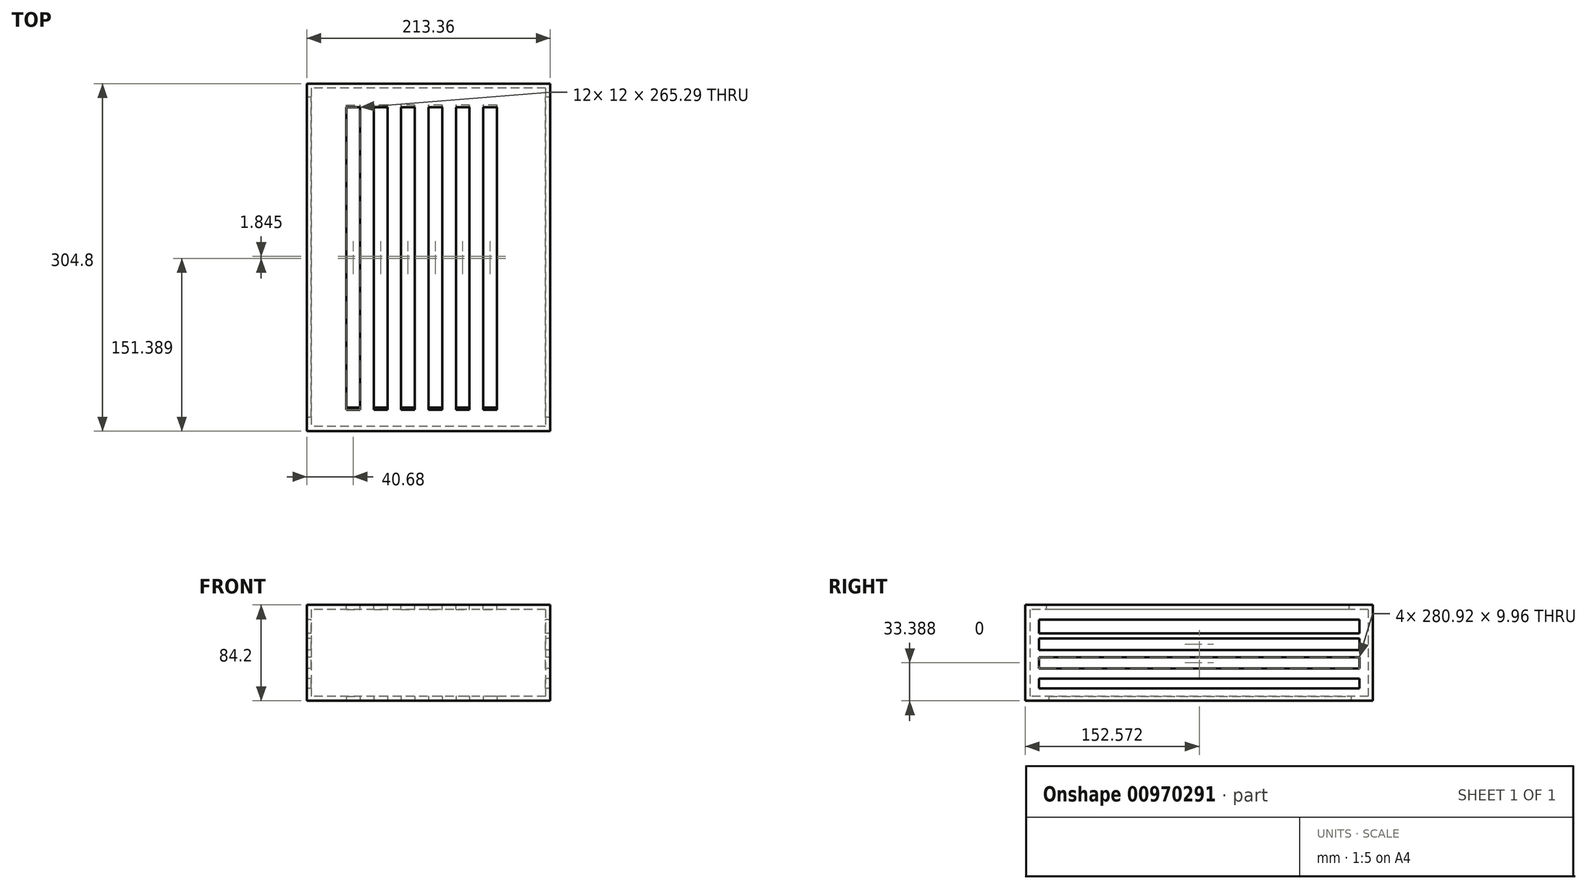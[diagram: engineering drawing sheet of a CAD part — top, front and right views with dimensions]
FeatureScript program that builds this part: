
annotation { "Feature Type Name" : "Feature", "Feature Type Description" : "" }
export const myFeature = defineFeature(function(context is Context, id is Id, definition is map)
    precondition{}
    {
        {
            var Q0;
            Q0=qCreatedBy(makeId("Top.planeOp"),FACE);
            var sketch = newSketch(context, id + "F0", { "sketchPlane" : qUnion([Q0])});
            skLineSegment(sketch, "E0.bottom", {"start": v(106.68, 152.4) * mm, "end": v(-106.68, 152.4) * mm});
            skLineSegment(sketch, "E0.top", {"start": v(106.68, -152.4) * mm, "end": v(-106.68, -152.4) * mm});
            skLineSegment(sketch, "E0.left", {"start": v(106.68, 152.4) * mm, "end": v(106.68, -152.4) * mm});
            skLineSegment(sketch, "E0.right", {"start": v(-106.68, 152.4) * mm, "end": v(-106.68, -152.4) * mm});
            skPoint(sketch, "E0.middle", {"position": v(0, 0) * mm});
            skLineSegment(sketch, "E1.bottom", {"start": v(102.68, 148.4) * mm, "end": v(-102.68, 148.4) * mm});
            skLineSegment(sketch, "E1.top", {"start": v(102.68, -148.4) * mm, "end": v(-102.68, -148.4) * mm});
            skLineSegment(sketch, "E1.left", {"start": v(102.68, 148.4) * mm, "end": v(102.68, -148.4) * mm});
            skLineSegment(sketch, "E1.right", {"start": v(-102.68, 148.4) * mm, "end": v(-102.68, -148.4) * mm});
            skSolve(sketch);
        }
        {
            var Q0;
            Q0=makeQuery(id+"F0.imprint","IMPRINT",FACE,{"disambiguationData":[TD([[makeQuery(id+"F0.imprint","IMPRINT",EDGE,{"derivedFrom":sQuery(id+"F0.wireOp",EDGE,"E1.bottom")}),1.0]])]});
            var Q1;
            Q1=makeQuery(id+"F0.imprint","IMPRINT",FACE,{"disambiguationData":[TD([[makeQuery(id+"F0.imprint","IMPRINT",EDGE,{"derivedFrom":sQuery(id+"F0.wireOp",EDGE,"E0.bottom")}),1.0]])]});
            extrude(context, id + "F1", {"entities" : qUnion([Q0, Q1]), "oppositeDirection" : true, "depth" : 4 * mm, "offsetDistance" : 25.4 * mm});
        }
        {
            var Q0;
            Q0=makeQuery(id+"F0.imprint","IMPRINT",FACE,{"disambiguationData":[TD([[makeQuery(id+"F0.imprint","IMPRINT",EDGE,{"derivedFrom":sQuery(id+"F0.wireOp",EDGE,"E0.bottom")}),1.0]])]});
            extrude(context, id + "F2", {"entities" : qUnion([Q0]), "operationType" : NewBodyOperationType.ADD, "depth" : 76.2 * mm, "offsetDistance" : 25.4 * mm});
        }
        {
            var Q0;
            Q0=makeQuery(id+"F2.opExtrude","CAP_FACE",FACE,{"disambiguationData":[OSD([sQuery(id+"F0.wireOp",EDGE,"E0.bottom"),sQuery(id+"F0.wireOp",EDGE,"E0.top"),sQuery(id+"F0.wireOp",EDGE,"E0.left"),sQuery(id+"F0.wireOp",EDGE,"E0.right"),sQuery(id+"F0.wireOp",EDGE,"E1.bottom"),sQuery(id+"F0.wireOp",EDGE,"E1.top"),sQuery(id+"F0.wireOp",EDGE,"E1.left"),sQuery(id+"F0.wireOp",EDGE,"E1.right")])],"isStart":false});
            var sketch = newSketch(context, id + "F3", { "sketchPlane" : qUnion([Q0])});
            skLineSegment(sketch, "E2.bottom", {"start": v(-106.68, 152.4) * mm, "end": v(106.68, 152.4) * mm});
            skLineSegment(sketch, "E2.top", {"start": v(-106.68, -152.4) * mm, "end": v(106.68, -152.4) * mm});
            skLineSegment(sketch, "E2.left", {"start": v(-106.68, 152.4) * mm, "end": v(-106.68, -152.4) * mm});
            skLineSegment(sketch, "E2.right", {"start": v(106.68, 152.4) * mm, "end": v(106.68, -152.4) * mm});
            skSolve(sketch);
        }
        {
            var Q0;
            Q0=makeQuery(id+"F3.imprint","IMPRINT",FACE,{"disambiguationData":[TD([[makeQuery(id+"F3.imprint","IMPRINT",EDGE,{"derivedFrom":makeQuery(id+"F2.opExtrude","CAP_EDGE",EDGE,{"disambiguationData":[OSD([sQuery(id+"F0.wireOp",EDGE,"E1.bottom")])],"isStart":false})}),1.0]])]});
            var Q1;
            Q1=makeQuery(id+"F3.imprint","IMPRINT",FACE,{"disambiguationData":[TD([[makeQuery(id+"F3.imprint","IMPRINT",EDGE,{"derivedFrom":sQuery(id+"F3.wireOp",EDGE,"E2.bottom")}),1.0]])]});
            extrude(context, id + "F4", {"entities" : qUnion([Q0, Q1]), "operationType" : NewBodyOperationType.ADD, "depth" : 4 * mm, "offsetDistance" : 25.4 * mm});
        }
        {
            var Q0;
            Q0=makeQuery(id+"F4.opExtrude","CAP_FACE",FACE,{"disambiguationData":[OSD([sQuery(id+"F3.wireOp",EDGE,"E2.bottom"),sQuery(id+"F3.wireOp",EDGE,"E2.top"),sQuery(id+"F3.wireOp",EDGE,"E2.left"),sQuery(id+"F3.wireOp",EDGE,"E2.right")])],"isStart":false});
            var sketch = newSketch(context, id + "F5", { "sketchPlane" : qUnion([Q0])});
            skLineSegment(sketch, "E3", {"start": v(-72, -133.65) * mm, "end": v(-72, 131.63) * mm});
            skLineSegment(sketch, "E4", {"start": v(-72, 131.63) * mm, "end": v(-60, 131.63) * mm});
            skLineSegment(sketch, "E5", {"start": v(-60, 131.63) * mm, "end": v(-60, -133.65) * mm});
            skLineSegment(sketch, "E6", {"start": v(-60, -133.65) * mm, "end": v(-72, -133.65) * mm});
            skLineSegment(sketch, "E7", {"start": v(60, -133.65) * mm, "end": v(60, 131.63) * mm});
            skLineSegment(sketch, "E8", {"start": v(60, 131.63) * mm, "end": v(48, 131.63) * mm});
            skLineSegment(sketch, "E9", {"start": v(48, 131.63) * mm, "end": v(48, -133.65) * mm});
            skLineSegment(sketch, "E10", {"start": v(48, -133.65) * mm, "end": v(60, -133.65) * mm});
            skLineSegment(sketch, "E11", {"start": v(36, -133.65) * mm, "end": v(36, 131.63) * mm});
            skLineSegment(sketch, "E12", {"start": v(36, 131.63) * mm, "end": v(24, 131.63) * mm});
            skLineSegment(sketch, "E13", {"start": v(24, 131.63) * mm, "end": v(24, -133.65) * mm});
            skLineSegment(sketch, "E14", {"start": v(24, -133.65) * mm, "end": v(36, -133.65) * mm});
            skLineSegment(sketch, "E15", {"start": v(12, -133.65) * mm, "end": v(12, 131.63) * mm});
            skLineSegment(sketch, "E16", {"start": v(12, 131.63) * mm, "end": v(0, 131.63) * mm});
            skLineSegment(sketch, "E17", {"start": v(0, 131.63) * mm, "end": v(0, -133.65) * mm});
            skLineSegment(sketch, "E18", {"start": v(0, -133.65) * mm, "end": v(12, -133.65) * mm});
            skLineSegment(sketch, "E19", {"start": v(-12, -133.65) * mm, "end": v(-12, 131.63) * mm});
            skPoint(sketch, "E19.startSnap0", {"position": v(6, -133.65) * mm});
            skLineSegment(sketch, "E20", {"start": v(-12, 131.63) * mm, "end": v(-24, 131.63) * mm});
            skLineSegment(sketch, "E21", {"start": v(-24, 131.63) * mm, "end": v(-24, -133.65) * mm});
            skLineSegment(sketch, "E22", {"start": v(-24, -133.65) * mm, "end": v(-12, -133.65) * mm});
            skLineSegment(sketch, "E23", {"start": v(-36, -133.65) * mm, "end": v(-36, 131.63) * mm});
            skLineSegment(sketch, "E24", {"start": v(-36, 131.63) * mm, "end": v(-48, 131.63) * mm});
            skLineSegment(sketch, "E25", {"start": v(-48, 131.63) * mm, "end": v(-48, -133.65) * mm});
            skLineSegment(sketch, "E26", {"start": v(-48, -133.65) * mm, "end": v(-36, -133.65) * mm});
            skLineSegment(sketch, "E27", {"start": v(-72, -133.65) * mm, "end": v(-106.68, -133.65) * mm});
            skLineSegment(sketch, "E28", {"start": v(-60, -133.65) * mm, "end": v(-48, -133.65) * mm});
            skLineSegment(sketch, "E29", {"start": v(-36, -133.65) * mm, "end": v(-24, -133.65) * mm});
            skLineSegment(sketch, "E30", {"start": v(-12, -133.65) * mm, "end": v(0, -133.65) * mm});
            skLineSegment(sketch, "E31", {"start": v(12, -133.65) * mm, "end": v(24, -133.65) * mm});
            skLineSegment(sketch, "E32", {"start": v(36, -133.65) * mm, "end": v(48, -133.65) * mm});
            skLineSegment(sketch, "E33", {"start": v(60, -133.65) * mm, "end": v(106.68, -133.65) * mm});
            skSolve(sketch);
        }
        {
            var Q0;
            Q0=makeQuery(id+"F5.imprint","IMPRINT",FACE,{"disambiguationData":[TD([[makeQuery(id+"F5.imprint","IMPRINT",EDGE,{"derivedFrom":sQuery(id+"F5.wireOp",EDGE,"E3")}),-1.0]])]});
            var Q1;
            Q1=makeQuery(id+"F5.imprint","IMPRINT",FACE,{"disambiguationData":[TD([[makeQuery(id+"F5.imprint","IMPRINT",EDGE,{"derivedFrom":sQuery(id+"F5.wireOp",EDGE,"E23")}),1.0]])]});
            var Q2;
            Q2=makeQuery(id+"F5.imprint","IMPRINT",FACE,{"disambiguationData":[TD([[makeQuery(id+"F5.imprint","IMPRINT",EDGE,{"derivedFrom":sQuery(id+"F5.wireOp",EDGE,"E19")}),1.0]])]});
            var Q3;
            Q3=makeQuery(id+"F5.imprint","IMPRINT",FACE,{"disambiguationData":[TD([[makeQuery(id+"F5.imprint","IMPRINT",EDGE,{"derivedFrom":sQuery(id+"F5.wireOp",EDGE,"E15")}),1.0]])]});
            var Q4;
            Q4=makeQuery(id+"F5.imprint","IMPRINT",FACE,{"disambiguationData":[TD([[makeQuery(id+"F5.imprint","IMPRINT",EDGE,{"derivedFrom":sQuery(id+"F5.wireOp",EDGE,"E11")}),1.0]])]});
            var Q5;
            Q5=makeQuery(id+"F5.imprint","IMPRINT",FACE,{"disambiguationData":[TD([[makeQuery(id+"F5.imprint","IMPRINT",EDGE,{"derivedFrom":sQuery(id+"F5.wireOp",EDGE,"E7")}),1.0]])]});
            extrude(context, id + "F6", {"entities" : qUnion([Q0, Q1, Q2, Q3, Q4, Q5]), "operationType" : NewBodyOperationType.REMOVE, "oppositeDirection" : true, "depth" : 5.08 * mm, "offsetDistance" : 25.4 * mm});
        }
        {
            var Q0;
            Q0=makeQuery(id+"F1.opExtrude","CAP_FACE",FACE,{"disambiguationData":[OSD([sQuery(id+"F0.wireOp",EDGE,"E0.bottom"),sQuery(id+"F0.wireOp",EDGE,"E0.top"),sQuery(id+"F0.wireOp",EDGE,"E0.left"),sQuery(id+"F0.wireOp",EDGE,"E0.right")])],"isStart":false});
            var sketch = newSketch(context, id + "F7", { "sketchPlane" : qUnion([Q0])});
            skLineSegment(sketch, "E34", {"start": v(-72, -133.48) * mm, "end": v(-72, 131.8) * mm});
            skLineSegment(sketch, "E35", {"start": v(-72, 131.8) * mm, "end": v(-60, 131.8) * mm});
            skLineSegment(sketch, "E36", {"start": v(-60, 131.8) * mm, "end": v(-60, -133.48) * mm});
            skLineSegment(sketch, "E37", {"start": v(-60, -133.48) * mm, "end": v(-72, -133.48) * mm});
            skLineSegment(sketch, "E38", {"start": v(60, -133.48) * mm, "end": v(60, 131.8) * mm});
            skLineSegment(sketch, "E39", {"start": v(60, 131.8) * mm, "end": v(48, 131.8) * mm});
            skLineSegment(sketch, "E40", {"start": v(48, 131.8) * mm, "end": v(48, -133.48) * mm});
            skLineSegment(sketch, "E41", {"start": v(48, -133.48) * mm, "end": v(60, -133.48) * mm});
            skLineSegment(sketch, "E42", {"start": v(36, -133.48) * mm, "end": v(36, 131.8) * mm});
            skLineSegment(sketch, "E43", {"start": v(36, 131.8) * mm, "end": v(24, 131.8) * mm});
            skLineSegment(sketch, "E44", {"start": v(24, 131.8) * mm, "end": v(24, -133.48) * mm});
            skLineSegment(sketch, "E45", {"start": v(24, -133.48) * mm, "end": v(36, -133.48) * mm});
            skLineSegment(sketch, "E46", {"start": v(12, -133.48) * mm, "end": v(12, 131.8) * mm});
            skLineSegment(sketch, "E47", {"start": v(12, 131.8) * mm, "end": v(0, 131.8) * mm});
            skLineSegment(sketch, "E48", {"start": v(0, 131.8) * mm, "end": v(0, -133.48) * mm});
            skLineSegment(sketch, "E49", {"start": v(0, -133.48) * mm, "end": v(12, -133.48) * mm});
            skLineSegment(sketch, "E50", {"start": v(-12, -133.48) * mm, "end": v(-12, 131.8) * mm});
            skPoint(sketch, "E50.startSnap0", {"position": v(6, -133.48) * mm});
            skLineSegment(sketch, "E51", {"start": v(-12, 131.8) * mm, "end": v(-24, 131.8) * mm});
            skLineSegment(sketch, "E52", {"start": v(-24, 131.8) * mm, "end": v(-24, -133.48) * mm});
            skLineSegment(sketch, "E53", {"start": v(-24, -133.48) * mm, "end": v(-12, -133.48) * mm});
            skLineSegment(sketch, "E54", {"start": v(-36, -133.48) * mm, "end": v(-36, 131.8) * mm});
            skLineSegment(sketch, "E55", {"start": v(-36, 131.8) * mm, "end": v(-48, 131.8) * mm});
            skLineSegment(sketch, "E56", {"start": v(-48, 131.8) * mm, "end": v(-48, -133.48) * mm});
            skLineSegment(sketch, "E57", {"start": v(-48, -133.48) * mm, "end": v(-36, -133.48) * mm});
            skLineSegment(sketch, "E58", {"start": v(-72, -133.48) * mm, "end": v(-106.68, -133.48) * mm});
            skLineSegment(sketch, "E59", {"start": v(-60, -133.48) * mm, "end": v(-48, -133.48) * mm});
            skLineSegment(sketch, "E60", {"start": v(-36, -133.48) * mm, "end": v(-24, -133.48) * mm});
            skLineSegment(sketch, "E61", {"start": v(-12, -133.48) * mm, "end": v(0, -133.48) * mm});
            skLineSegment(sketch, "E62", {"start": v(12, -133.48) * mm, "end": v(24, -133.48) * mm});
            skLineSegment(sketch, "E63", {"start": v(36, -133.48) * mm, "end": v(48, -133.48) * mm});
            skLineSegment(sketch, "E64", {"start": v(60, -133.48) * mm, "end": v(106.68, -133.48) * mm});
            skSolve(sketch);
        }
        {
            var Q0;
            Q0=makeQuery(id+"F7.imprint","IMPRINT",FACE,{"disambiguationData":[TD([[makeQuery(id+"F7.imprint","IMPRINT",EDGE,{"derivedFrom":sQuery(id+"F7.wireOp",EDGE,"E34")}),-1.0]])]});
            var Q1;
            Q1=makeQuery(id+"F7.imprint","IMPRINT",FACE,{"disambiguationData":[TD([[makeQuery(id+"F7.imprint","IMPRINT",EDGE,{"derivedFrom":sQuery(id+"F7.wireOp",EDGE,"E54")}),1.0]])]});
            var Q2;
            Q2=makeQuery(id+"F7.imprint","IMPRINT",FACE,{"disambiguationData":[TD([[makeQuery(id+"F7.imprint","IMPRINT",EDGE,{"derivedFrom":sQuery(id+"F7.wireOp",EDGE,"E50")}),1.0]])]});
            var Q3;
            Q3=makeQuery(id+"F7.imprint","IMPRINT",FACE,{"disambiguationData":[TD([[makeQuery(id+"F7.imprint","IMPRINT",EDGE,{"derivedFrom":sQuery(id+"F7.wireOp",EDGE,"E46")}),1.0]])]});
            var Q4;
            Q4=makeQuery(id+"F7.imprint","IMPRINT",FACE,{"disambiguationData":[TD([[makeQuery(id+"F7.imprint","IMPRINT",EDGE,{"derivedFrom":sQuery(id+"F7.wireOp",EDGE,"E42")}),1.0]])]});
            var Q5;
            Q5=makeQuery(id+"F7.imprint","IMPRINT",FACE,{"disambiguationData":[TD([[makeQuery(id+"F7.imprint","IMPRINT",EDGE,{"derivedFrom":sQuery(id+"F7.wireOp",EDGE,"E38")}),1.0]])]});
            extrude(context, id + "F8", {"entities" : qUnion([Q0, Q1, Q2, Q3, Q4, Q5]), "operationType" : NewBodyOperationType.REMOVE, "oppositeDirection" : true, "depth" : 5.08 * mm, "offsetDistance" : 25.4 * mm});
        }
        {
            var Q0;
            {var subQ0=sQuery(id+"F0.wireOp",EDGE,"E0.right");Q0=makeQuery(id+"F4.boolean.opBoolean","MERGE",FACE,{"derivedFrom":[makeQuery(id+"F2.boolean.opBoolean","MERGE",FACE,{"derivedFrom":[makeQuery(id+"F1.opExtrude","SWEPT_FACE",FACE,{"disambiguationData":[OSD([subQ0])]}),makeQuery(id+"F2.opExtrude","SWEPT_FACE",FACE,{"disambiguationData":[OSD([subQ0])]})]}),makeQuery(id+"F4.opExtrude","SWEPT_FACE",FACE,{"disambiguationData":[OSD([sQuery(id+"F3.wireOp",EDGE,"E2.left")])]})]});}
            var sketch = newSketch(context, id + "F9", { "sketchPlane" : qUnion([Q0])});
            skLineSegment(sketch, "E65", {"start": v(-140.63, 6.9) * mm, "end": v(140.29, 6.9) * mm});
            skLineSegment(sketch, "E66", {"start": v(140.29, 6.9) * mm, "end": v(140.29, 15.36) * mm});
            skLineSegment(sketch, "E67", {"start": v(140.29, 15.36) * mm, "end": v(-140.63, 15.36) * mm});
            skLineSegment(sketch, "E68", {"start": v(-140.63, 15.36) * mm, "end": v(-140.63, 6.9) * mm});
            skLineSegment(sketch, "E69", {"start": v(-140.63, 24.4) * mm, "end": v(140.29, 24.4) * mm});
            skLineSegment(sketch, "E70", {"start": v(140.29, 24.4) * mm, "end": v(140.29, 34.37) * mm});
            skLineSegment(sketch, "E71", {"start": v(140.29, 34.37) * mm, "end": v(-140.63, 34.37) * mm});
            skLineSegment(sketch, "E72", {"start": v(-140.63, 34.37) * mm, "end": v(-140.63, 24.4) * mm});
            skLineSegment(sketch, "E73", {"start": v(-140.63, 67.26) * mm, "end": v(140.29, 67.26) * mm});
            skLineSegment(sketch, "E74", {"start": v(140.29, 67.26) * mm, "end": v(140.29, 55.19) * mm});
            skLineSegment(sketch, "E75", {"start": v(140.29, 55.19) * mm, "end": v(-140.63, 55.19) * mm});
            skLineSegment(sketch, "E76", {"start": v(-140.63, 55.19) * mm, "end": v(-140.63, 67.26) * mm});
            skLineSegment(sketch, "E77", {"start": v(-140.63, 40.7) * mm, "end": v(140.29, 40.7) * mm});
            skLineSegment(sketch, "E78", {"start": v(140.29, 40.7) * mm, "end": v(140.29, 50.66) * mm});
            skLineSegment(sketch, "E79", {"start": v(140.29, 50.66) * mm, "end": v(-140.63, 50.66) * mm});
            skLineSegment(sketch, "E80", {"start": v(-140.63, 50.66) * mm, "end": v(-140.63, 40.7) * mm});
            skSolve(sketch);
        }
        {
            var Q0;
            Q0=makeQuery(id+"F9.imprint","IMPRINT",FACE,{"disambiguationData":[TD([[makeQuery(id+"F9.imprint","IMPRINT",EDGE,{"derivedFrom":sQuery(id+"F9.wireOp",EDGE,"E73")}),-1.0]])]});
            var Q1;
            Q1=makeQuery(id+"F9.imprint","IMPRINT",FACE,{"disambiguationData":[TD([[makeQuery(id+"F9.imprint","IMPRINT",EDGE,{"derivedFrom":sQuery(id+"F9.wireOp",EDGE,"E77")}),1.0]])]});
            var Q2;
            Q2=makeQuery(id+"F9.imprint","IMPRINT",FACE,{"disambiguationData":[TD([[makeQuery(id+"F9.imprint","IMPRINT",EDGE,{"derivedFrom":sQuery(id+"F9.wireOp",EDGE,"E69")}),1.0]])]});
            var Q3;
            Q3=makeQuery(id+"F9.imprint","IMPRINT",FACE,{"disambiguationData":[TD([[makeQuery(id+"F9.imprint","IMPRINT",EDGE,{"derivedFrom":sQuery(id+"F9.wireOp",EDGE,"E65")}),1.0]])]});
            extrude(context, id + "F10", {"entities" : qUnion([Q0, Q1, Q2, Q3]), "operationType" : NewBodyOperationType.REMOVE, "oppositeDirection" : true, "depth" : 287.02 * mm, "offsetDistance" : 25.4 * mm});
        }
    });
